# Revit family: Roof-Access_Drain_Acudor_Retrofit
name_source: partatom
category: Plumbing Fixtures
units: mm (PartAtom-declared; Revit-internal decimal feet)

## family parameters
Always vertical = No
Cut with Voids When Loaded = No
Enable Cutting in Views = No
Maintain Annotation Orientation = No
Part Type = Normal
Room Calculation Point = No
Round Connector Dimension = Use Diameter
Shared = No
Work Plane-Based = Yes

## types (9) — shared parameters
Default Elevation = 0' - 0"
Door Height = 0' - 5 1/4"
Door Width = 1' - 5 1/2"
Opening Height = 0' - 0"
Opening Width = 0' - 0"
Revision = R1_01-2014
Standards Conformance = CSA-B79  ;  ASME 112-6-4
Unit Depth = 0' - 1"
Unit Height = 0' - 5 3/4"
Unit Width = 1' - 6"
zero-valued in all types: Expected Lifespan (Years), Maintenance Schedule (Months), Warranty Duration (Years)

## per-type parameters (varying)
| type | Description | Drain OD | Drain Pipe Connection Size | Model | drainor |
| Recessed Deck 5.75in | Acudor Retrofit Aluminum Roof Drain - ARDR05 as Specified | 6" | 6" | ARDR05 | 0' - 2 15/16" |
| Recessed Deck 4.75in | Acudor Retrofit Aluminum Roof Drain - ARDR04 as Specified | 5" | 5" | ARDR04 | 0' - 2 7/16" |
| Recessed Deck 3.75in | Acudor Retrofit Aluminum Roof Drain - ARDR03 as Specified | 4" | 4" | ARDR03 | 0' - 1 15/16" |
| Recessed Deck 2.75in | Acudor Retrofit Aluminum Roof Drain - ARDR02 as Specified | 3" | 3" | ARDR02 | 0' - 1 7/16" |
| Flat Deck 5.75in | Acudor Retrofit Aluminum Roof Drain - ARDF05 as Specified | 6" | 6" | ARDF05 | 0' - 2 15/16" |
| Flat Deck 4.75in | Acudor Retrofit Aluminum Roof Drain - ARDF04 as Specified | 5" | 5" | ARDF04 | 0' - 2 7/16" |
| Flat Deck 3.75in | Acudor Retrofit Aluminum Roof Drain - ARDF03 as Specified | 4" | 4" | ARDF03 | 0' - 1 15/16" |
| Flat Deck 2.75in | Acudor Retrofit Aluminum Roof Drain - ARDF02 as Specified | 3" | 3" | ARDF02 | 0' - 1 7/16" |
| Flat Deck 1.75in | Acudor Retrofit Aluminum Roof Drain - ARDF01 as Specified | 2" | 2" | ARDF01 | 0' - 0 15/16" |

## geometry (parser evidence)
native form markers: Sweep x1
no freeform markers — native parametric forms only
